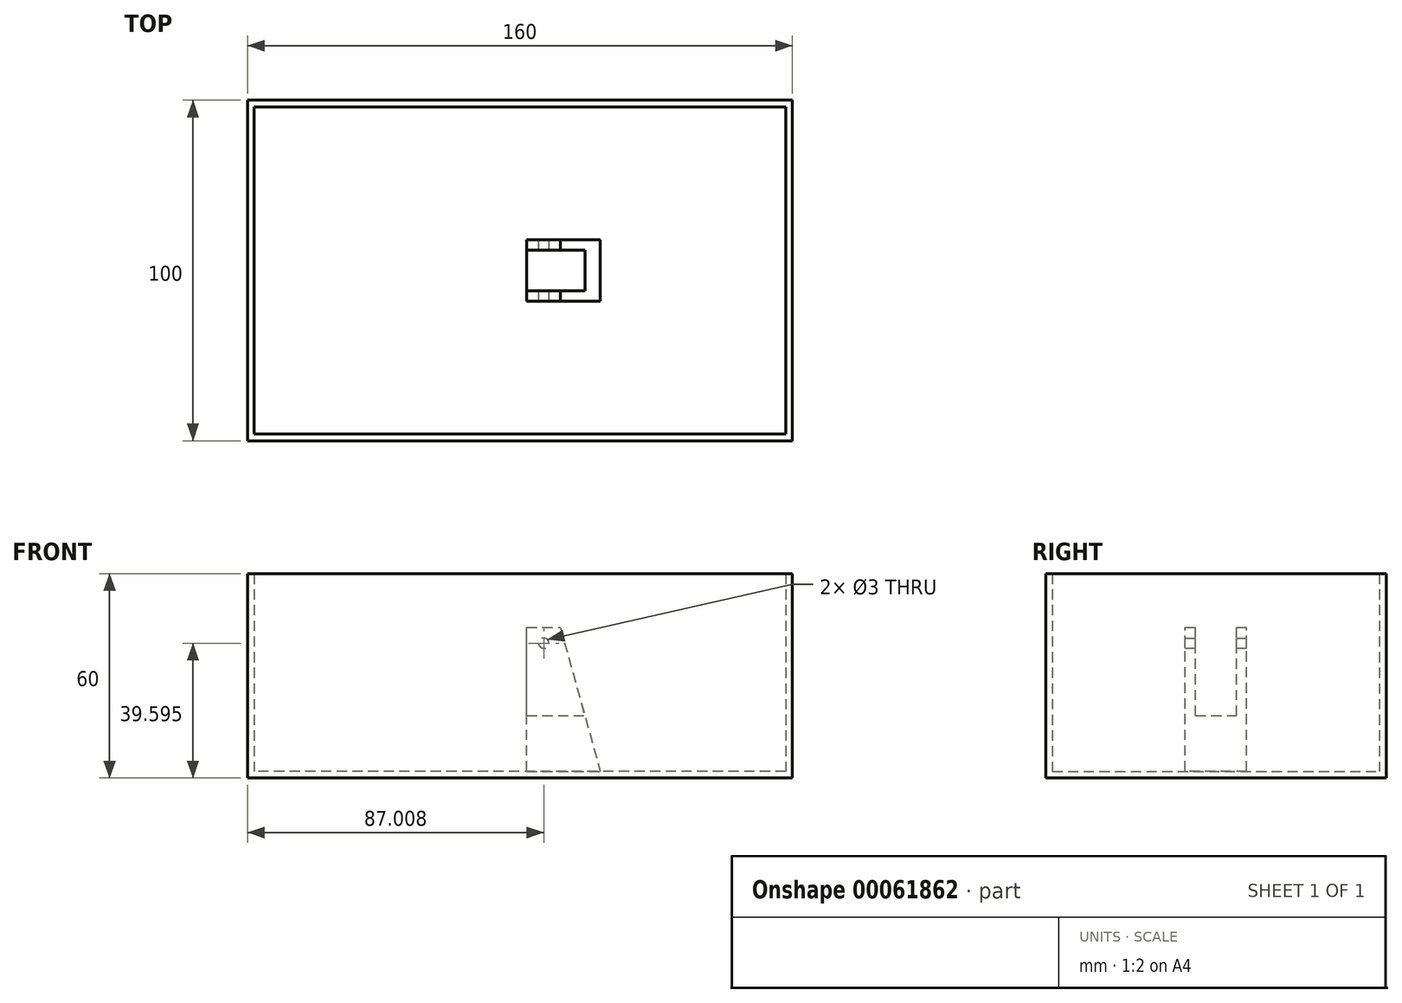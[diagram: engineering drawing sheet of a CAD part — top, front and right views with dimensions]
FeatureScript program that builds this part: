
annotation { "Feature Type Name" : "Feature", "Feature Type Description" : "" }
export const myFeature = defineFeature(function(context is Context, id is Id, definition is map)
    precondition{}
    {
        {
            var Q0;
            Q0=qCreatedBy(makeId("Top.planeOp"),FACE);
            var sketch = newSketch(context, id + "F0", { "sketchPlane" : qUnion([Q0])});
            skLineSegment(sketch, "E0.rect.bottom", {"start": v(80, -50) * mm, "end": v(-80, -50) * mm});
            skLineSegment(sketch, "E0.rect.top", {"start": v(80, 50) * mm, "end": v(-80, 50) * mm});
            skLineSegment(sketch, "E0.rect.left", {"start": v(80, -50) * mm, "end": v(80, 50) * mm});
            skLineSegment(sketch, "E0.rect.right", {"start": v(-80, -50) * mm, "end": v(-80, 50) * mm});
            skPoint(sketch, "E0.rect.middle", {"position": v(0, 0) * mm});
            skSolve(sketch);
        }
        {
            assignVariable(context, id + "F1", {"name" : "box_height", "anyValue" : 60});
        }
        {
            var Q0;
            Q0 = qSketchRegion(id + "F0", true);
            extrude(context, id + "F2", {"entities" : qUnion([Q0]), "depth" : (getVariable(context, 'box_height')) * mm});
        }
        {
            var Q0;
            Q0=makeQuery(id+"F2.opExtrude","CAP_FACE",FACE,{"disambiguationData":[OSD([sQuery(id+"F0.wireOp",EDGE,"E0.rect.bottom"),sQuery(id+"F0.wireOp",EDGE,"E0.rect.top"),sQuery(id+"F0.wireOp",EDGE,"E0.rect.left"),sQuery(id+"F0.wireOp",EDGE,"E0.rect.right")])],"isStart":false});
            shell(context, id + "F3", {"entities" : qUnion([Q0]), "thickness" : 2 * mm});
        }
        {
            var Q0;
            Q0=qCreatedBy(makeId("Front.planeOp"),FACE);
            var sketch = newSketch(context, id + "F4", { "sketchPlane" : qUnion([Q0])});
            skLineSegment(sketch, "E1", {"start": v(1.98, 0) * mm, "end": v(1.98, 44.28) * mm});
            skLineSegment(sketch, "E2", {"start": v(1.98, 44.28) * mm, "end": v(11.82, 44.28) * mm});
            skLineSegment(sketch, "E3", {"start": v(11.82, 44.28) * mm, "end": v(24.15, 0) * mm});
            skLineSegment(sketch, "E4", {"start": v(24.15, 0) * mm, "end": v(1.98, 0) * mm});
            skCircle(sketch, "E5", {"center": v(7, 39.6) * mm, "radius": 1.5 * mm});
            skSolve(sketch);
        }
        {
            var Q0;
            Q0 = qSketchRegion(id + "F4", true);
            extrude(context, id + "F5", {"entities" : qUnion([Q0]), "operationType" : NewBodyOperationType.ADD, "endBound" : BoundingType.SYMMETRIC, "depth" : 18 * mm});
        }
        {
            var Q0;
            Q0=makeQuery(id+"F5.opExtrude","SWEPT_FACE",FACE,{"disambiguationData":[OSD([sQuery(id+"F4.wireOp",EDGE,"E2")])]});
            var sketch = newSketch(context, id + "F6", { "sketchPlane" : qUnion([Q0])});
            skLineSegment(sketch, "E6.bottom", {"start": v(-29.54, 6) * mm, "end": v(37.35, 6) * mm});
            skLineSegment(sketch, "E6.top", {"start": v(-29.54, -6) * mm, "end": v(37.35, -6) * mm});
            skLineSegment(sketch, "E6.left", {"start": v(-29.54, 6) * mm, "end": v(-29.54, -6) * mm});
            skLineSegment(sketch, "E6.right", {"start": v(37.35, 6) * mm, "end": v(37.35, -6) * mm});
            skLineSegment(sketch, "E7", {"start": v(-51.64, 0) * mm, "end": v(42.8, 0) * mm, "construction": true});
            skPoint(sketch, "E7.endSnap0", {"position": v(-29.54, 0) * mm});
            skSolve(sketch);
        }
        {
            var Q0;
            Q0 = qSketchRegion(id + "F6", true);
            extrude(context, id + "F7", {"entities" : qUnion([Q0]), "operationType" : NewBodyOperationType.REMOVE, "oppositeDirection" : true, "depth" : 26 * mm});
        }
    });
